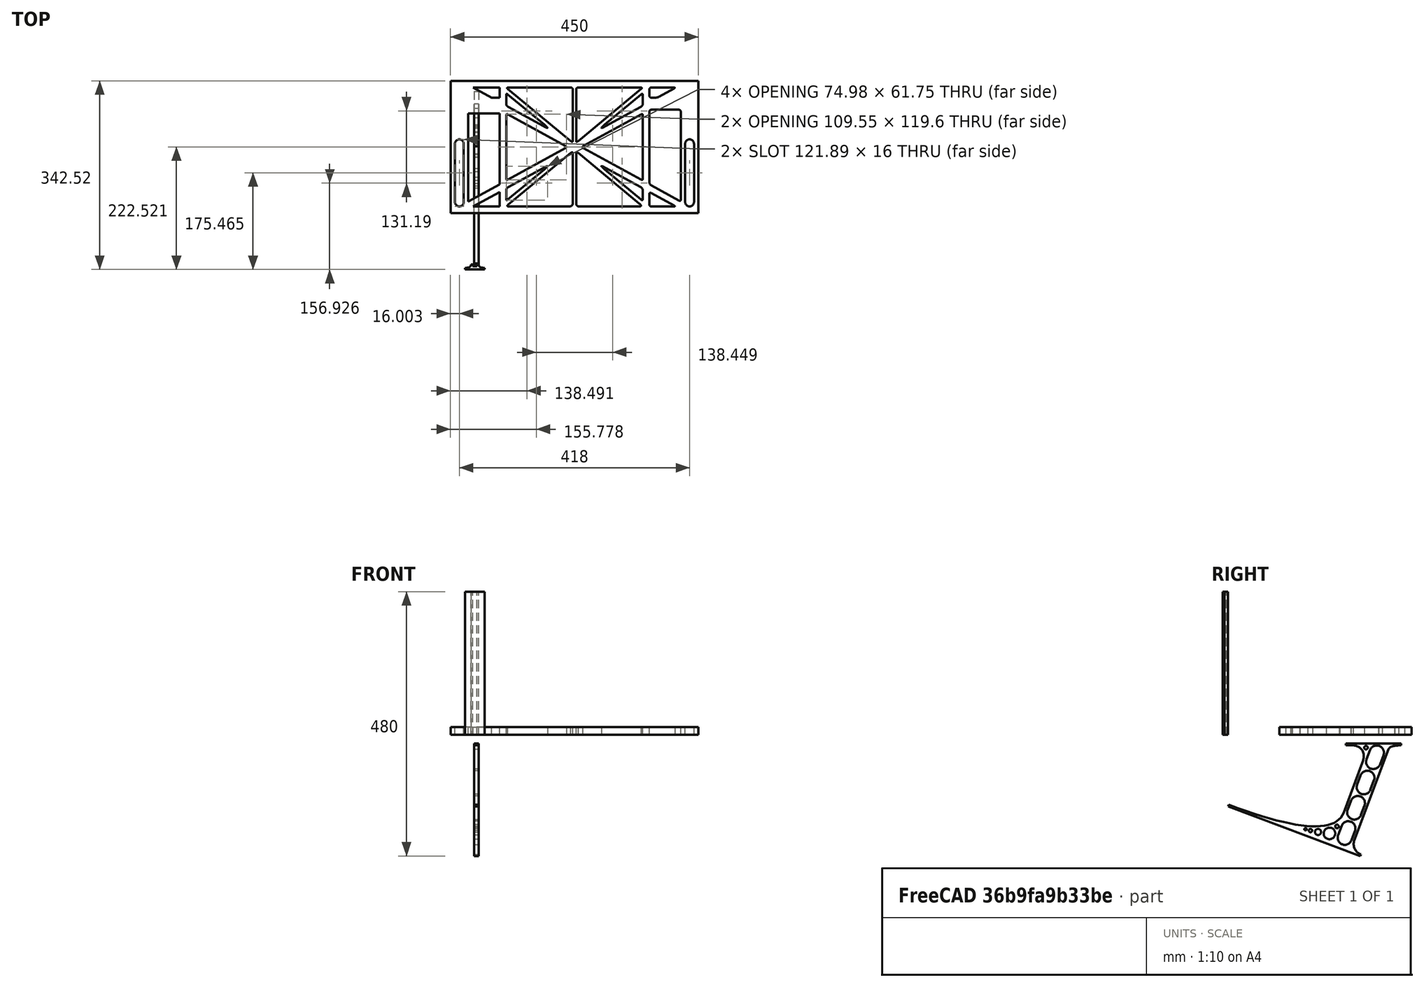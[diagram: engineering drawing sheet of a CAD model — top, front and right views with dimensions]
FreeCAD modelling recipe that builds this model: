
FCSTD DOCUMENT  (FreeCAD 0.19R0.19.2)
Label: laptopStand112
License: All rights reserved
LicenseURL: http://en.wikipedia.org/wiki/All_rights_reserved
objects: Sketcher::SketchObject×3, Part::Extrusion×3
note: 6 computed .brp shape members not serialized (recipe doc carries the construction recipe); baked Part::Feature solids carry a one-line shape summary decoded from their .brp

FEATURE [Sketcher::SketchObject] Sketch
  FullyConstrained = true
  sketch-geometry (310):
    g0: LineSegment StartX=-10.9272 StartY=-82.7794 StartZ=0 EndX=46.0728 EndY=-51.4823 EndZ=0
    g1: LineSegment StartX=-10.9272 StartY=77.3346 StartZ=0 EndX=-10.9272 EndY=-82.7794 EndZ=0
    g2: LineSegment StartX=-1.92719 StartY=-91.7794 StartZ=0 EndX=46.0728 EndY=-91.7794 EndZ=0
    g3: LineSegment StartX=46.0728 StartY=-65.424 StartZ=0 EndX=-1.92719 EndY=-91.7794 EndZ=0
    g4: LineSegment StartX=46.0728 StartY=-65.424 StartZ=0 EndX=46.0728 EndY=-91.7794 EndZ=0
    g5: LineSegment StartX=46.0728 StartY=77.3346 StartZ=0 EndX=46.0728 EndY=-51.4823 EndZ=0
    g6: LineSegment StartX=-42.9272 StartY=136.221 StartZ=0 EndX=-42.9272 EndY=-103.779 EndZ=0
    g7: LineSegment StartX=407.073 StartY=136.221 StartZ=0 EndX=407.073 EndY=-103.779 EndZ=0
    g8: ArcOfCircle CenterX=-26.9272 CenterY=22.1087 CenterZ=0 NormalX=0 NormalY=0 NormalZ=1 AngleXU=0 Radius=8 StartAngle=1e-16 EndAngle=3.14159
    g9: ArcOfCircle CenterX=-26.9272 CenterY=-83.7794 CenterZ=0 NormalX=0 NormalY=0 NormalZ=1 AngleXU=0 Radius=8 StartAngle=3.14159 EndAngle=6.28319
    g10: LineSegment StartX=-34.9272 StartY=22.1087 StartZ=0 EndX=-34.9272 EndY=-83.7794 EndZ=0
    g11: LineSegment StartX=-18.9272 StartY=22.1087 StartZ=0 EndX=-18.9272 EndY=-83.7794 EndZ=0
    g12: ArcOfCircle CenterX=391.073 CenterY=22.1087 CenterZ=0 NormalX=0 NormalY=0 NormalZ=1 AngleXU=0 Radius=8 StartAngle=-4.4e-15 EndAngle=3.14159
    g13: LineSegment StartX=399.073 StartY=22.1087 StartZ=0 EndX=399.073 EndY=-83.7794 EndZ=0
    g14: LineSegment StartX=383.073 StartY=22.1087 StartZ=0 EndX=383.073 EndY=-83.7794 EndZ=0
    g15: ArcOfCircle CenterX=391.073 CenterY=-83.7794 CenterZ=0 NormalX=0 NormalY=0 NormalZ=1 AngleXU=0 Radius=8 StartAngle=3.14159 EndAngle=6.28319
    g16: Circle CenterX=175.022 CenterY=27.0628 CenterZ=0 NormalX=0 NormalY=0 NormalZ=1 AngleXU=0 Radius=1
    g17: Circle CenterX=179.022 CenterY=24.8665 CenterZ=0 NormalX=0 NormalY=0 NormalZ=1 AngleXU=0 Radius=1
    g18: Circle CenterX=179.022 CenterY=27.0628 CenterZ=0 NormalX=0 NormalY=0 NormalZ=1 AngleXU=0 Radius=1
    g19: BSplineCurve PolesCount=3 KnotsCount=2 Degree=2 IsPeriodic=0
    g20: GeomPoint X=175.022 Y=27.0628 Z=0
    g21: GeomPoint X=179.022 Y=27.0628 Z=0
    g22: Circle CenterX=189.124 CenterY=27.0628 CenterZ=0 NormalX=0 NormalY=0 NormalZ=1 AngleXU=0 Radius=1
    g23: Circle CenterX=185.124 CenterY=24.8665 CenterZ=0 NormalX=0 NormalY=0 NormalZ=1 AngleXU=0 Radius=1
    g24: Circle CenterX=185.124 CenterY=27.0628 CenterZ=0 NormalX=0 NormalY=0 NormalZ=1 AngleXU=0 Radius=1
    g25: BSplineCurve PolesCount=3 KnotsCount=2 Degree=2 IsPeriodic=0
    g26: GeomPoint X=189.124 Y=27.0628 Z=0
    g27: GeomPoint X=185.124 Y=27.0628 Z=0
    g28: Circle CenterX=175.022 CenterY=5.37834 CenterZ=0 NormalX=0 NormalY=0 NormalZ=1 AngleXU=0 Radius=1
    g29: Circle CenterX=179.022 CenterY=7.57463 CenterZ=0 NormalX=0 NormalY=0 NormalZ=1 AngleXU=0 Radius=1
    g30: Circle CenterX=179.022 CenterY=5.34704 CenterZ=0 NormalX=0 NormalY=0 NormalZ=1 AngleXU=0 Radius=1
    g31: BSplineCurve PolesCount=3 KnotsCount=2 Degree=2 IsPeriodic=0
    g32: GeomPoint X=175.022 Y=5.37834 Z=0
    g33: GeomPoint X=179.022 Y=5.34704 Z=0
    g34: Circle CenterX=189.124 CenterY=5.37834 CenterZ=0 NormalX=0 NormalY=0 NormalZ=1 AngleXU=0 Radius=1
    g35: Circle CenterX=185.124 CenterY=7.57463 CenterZ=0 NormalX=0 NormalY=0 NormalZ=1 AngleXU=0 Radius=1
    g36: Circle CenterX=185.124 CenterY=5.34704 CenterZ=0 NormalX=0 NormalY=0 NormalZ=1 AngleXU=0 Radius=1
    g37: BSplineCurve PolesCount=3 KnotsCount=2 Degree=2 IsPeriodic=0
    g38: GeomPoint X=189.124 Y=5.37834 Z=0
    g39: GeomPoint X=185.124 Y=5.34704 Z=0
    g40: Circle CenterX=165.871 CenterY=18.1458 CenterZ=0 NormalX=0 NormalY=0 NormalZ=1 AngleXU=0 Radius=1
    g41: Circle CenterX=169.377 CenterY=16.2206 CenterZ=0 NormalX=0 NormalY=0 NormalZ=1 AngleXU=0 Radius=1
    g42: Circle CenterX=165.871 CenterY=14.2954 CenterZ=0 NormalX=0 NormalY=0 NormalZ=1 AngleXU=0 Radius=1
    g43: BSplineCurve PolesCount=3 KnotsCount=2 Degree=2 IsPeriodic=0
    g44: GeomPoint X=165.871 Y=18.1458 Z=0
    g45: GeomPoint X=165.871 Y=14.2954 Z=0
    g46: Circle CenterX=198.275 CenterY=18.1458 CenterZ=0 NormalX=0 NormalY=0 NormalZ=1 AngleXU=0 Radius=1
    g47: Circle CenterX=194.768 CenterY=16.2206 CenterZ=0 NormalX=0 NormalY=0 NormalZ=1 AngleXU=0 Radius=1
    g48: Circle CenterX=198.275 CenterY=14.2954 CenterZ=0 NormalX=0 NormalY=0 NormalZ=1 AngleXU=0 Radius=1
    g49: BSplineCurve PolesCount=3 KnotsCount=2 Degree=2 IsPeriodic=0
    g50: GeomPoint X=198.275 Y=18.1458 Z=0
    g51: GeomPoint X=198.275 Y=14.2954 Z=0
    g52: LineSegment StartX=407.073 StartY=-103.779 StartZ=0 EndX=-42.9272 EndY=-103.779 EndZ=0
    g53: LineSegment StartX=407.073 StartY=136.221 StartZ=0 EndX=-42.9272 EndY=136.221 EndZ=0
    g54: LineSegment StartX=46.0728 StartY=77.3346 StartZ=0 EndX=-10.9272 EndY=77.3346 EndZ=0
    g55: LineSegment StartX=46.0728 StartY=105.865 StartZ=0 EndX=31.5028 EndY=105.865 EndZ=0
    g56: LineSegment StartX=46.0728 StartY=124.221 StartZ=0 EndX=46.0728 EndY=105.865 EndZ=0
    g57: LineSegment StartX=-1.92719 StartY=124.221 StartZ=0 EndX=31.5028 EndY=105.865 EndZ=0
    g58: LineSegment StartX=46.0728 StartY=124.221 StartZ=0 EndX=-1.92719 EndY=124.221 EndZ=0
    g59: Circle CenterX=125.607 CenterY=54.1951 CenterZ=0 NormalX=0 NormalY=0 NormalZ=1 AngleXU=0 Radius=1
    g60: Circle CenterX=139.632 CenterY=46.4944 CenterZ=0 NormalX=0 NormalY=0 NormalZ=1 AngleXU=0 Radius=1
    g61: Circle CenterX=127.326 CenterY=56.7187 CenterZ=0 NormalX=0 NormalY=0 NormalZ=1 AngleXU=0 Radius=1
    g62: BSplineCurve PolesCount=3 KnotsCount=2 Degree=2 IsPeriodic=0
    g63: GeomPoint X=125.607 Y=54.1951 Z=0
    g64: GeomPoint X=127.326 Y=56.7187 Z=0
    g65: Circle CenterX=236.821 CenterY=56.7187 CenterZ=0 NormalX=0 NormalY=0 NormalZ=1 AngleXU=0 Radius=1
    g66: Circle CenterX=224.513 CenterY=46.4944 CenterZ=0 NormalX=0 NormalY=0 NormalZ=1 AngleXU=0 Radius=1
    g67: Circle CenterX=238.538 CenterY=54.1951 CenterZ=0 NormalX=0 NormalY=0 NormalZ=1 AngleXU=0 Radius=1
    g68: BSplineCurve PolesCount=3 KnotsCount=2 Degree=2 IsPeriodic=0
    g69: GeomPoint X=236.821 Y=56.7187 Z=0
    g70: GeomPoint X=238.538 Y=54.1951 Z=0
    g71: Circle CenterX=238.538 CenterY=-21.7539 CenterZ=0 NormalX=0 NormalY=0 NormalZ=1 AngleXU=0 Radius=1
    g72: Circle CenterX=224.513 CenterY=-14.0532 CenterZ=0 NormalX=0 NormalY=0 NormalZ=1 AngleXU=0 Radius=1
    g73: Circle CenterX=236.821 CenterY=-24.2775 CenterZ=0 NormalX=0 NormalY=0 NormalZ=1 AngleXU=0 Radius=1
    g74: BSplineCurve PolesCount=3 KnotsCount=2 Degree=2 IsPeriodic=0
    g75: GeomPoint X=238.538 Y=-21.7539 Z=0
    g76: GeomPoint X=236.821 Y=-24.2775 Z=0
    g77: Circle CenterX=125.607 CenterY=-21.7539 CenterZ=0 NormalX=0 NormalY=0 NormalZ=1 AngleXU=0 Radius=1
    g78: Circle CenterX=139.632 CenterY=-14.0532 CenterZ=0 NormalX=0 NormalY=0 NormalZ=1 AngleXU=0 Radius=1
    g79: Circle CenterX=127.325 CenterY=-24.2775 CenterZ=0 NormalX=0 NormalY=0 NormalZ=1 AngleXU=0 Radius=1
    g80: BSplineCurve PolesCount=3 KnotsCount=2 Degree=2 IsPeriodic=0
    g81: GeomPoint X=125.607 Y=-21.7539 Z=0
    g82: GeomPoint X=127.325 Y=-24.2775 Z=0
    g83: Circle CenterX=302.996 CenterY=111.695 CenterZ=0 NormalX=0 NormalY=0 NormalZ=1 AngleXU=0 Radius=1
    g84: Circle CenterX=306.073 CenterY=114.251 CenterZ=0 NormalX=0 NormalY=0 NormalZ=1 AngleXU=0 Radius=1
    g85: Circle CenterX=306.073 CenterY=110.251 CenterZ=0 NormalX=0 NormalY=0 NormalZ=1 AngleXU=0 Radius=1
    g86: BSplineCurve PolesCount=3 KnotsCount=2 Degree=2 IsPeriodic=0
    g87: GeomPoint X=302.996 Y=111.695 Z=0
    g88: GeomPoint X=306.073 Y=110.251 Z=0
    g89: Circle CenterX=306.073 CenterY=95.2763 CenterZ=0 NormalX=0 NormalY=0 NormalZ=1 AngleXU=0 Radius=1
    g90: Circle CenterX=306.073 CenterY=91.2763 CenterZ=0 NormalX=0 NormalY=0 NormalZ=1 AngleXU=0 Radius=1
    g91: Circle CenterX=302.567 CenterY=89.3511 CenterZ=0 NormalX=0 NormalY=0 NormalZ=1 AngleXU=0 Radius=1
    g92: BSplineCurve PolesCount=3 KnotsCount=2 Degree=2 IsPeriodic=0
    g93: GeomPoint X=306.073 Y=95.2763 Z=0
    g94: GeomPoint X=302.567 Y=89.3511 Z=0
    g95: LineSegment StartX=306.073 StartY=110.251 StartZ=0 EndX=306.073 EndY=95.2763 EndZ=0
    g96: LineSegment StartX=302.996 StartY=111.695 StartZ=0 EndX=236.821 EndY=56.7187 EndZ=0
    g97: LineSegment StartX=238.538 StartY=54.1951 StartZ=0 EndX=302.567 EndY=89.3511 EndZ=0
    g98: Circle CenterX=61.1496 CenterY=111.695 CenterZ=0 NormalX=0 NormalY=0 NormalZ=1 AngleXU=0 Radius=1
    g99: Circle CenterX=58.0728 CenterY=114.251 CenterZ=0 NormalX=0 NormalY=0 NormalZ=1 AngleXU=0 Radius=1
    g100: Circle CenterX=58.0728 CenterY=110.251 CenterZ=0 NormalX=0 NormalY=0 NormalZ=1 AngleXU=0 Radius=1
    g101: BSplineCurve PolesCount=3 KnotsCount=2 Degree=2 IsPeriodic=0
    g102: GeomPoint X=61.1496 Y=111.695 Z=0
    g103: GeomPoint X=58.0728 Y=110.251 Z=0
    g104: Circle CenterX=61.5791 CenterY=89.3511 CenterZ=0 NormalX=0 NormalY=0 NormalZ=1 AngleXU=0 Radius=1
    g105: Circle CenterX=58.0728 CenterY=91.2763 CenterZ=0 NormalX=0 NormalY=0 NormalZ=1 AngleXU=0 Radius=1
    g106: Circle CenterX=58.0728 CenterY=95.2763 CenterZ=0 NormalX=0 NormalY=0 NormalZ=1 AngleXU=0 Radius=1
    g107: BSplineCurve PolesCount=3 KnotsCount=2 Degree=2 IsPeriodic=0
    g108: GeomPoint X=61.5791 Y=89.3511 Z=0
    g109: GeomPoint X=58.0728 Y=95.2763 Z=0
    g110: LineSegment StartX=58.0728 StartY=110.251 StartZ=0 EndX=58.0728 EndY=95.2763 EndZ=0
    g111: LineSegment StartX=61.1496 StartY=111.695 StartZ=0 EndX=127.326 EndY=56.7187 EndZ=0
    g112: LineSegment StartX=125.607 StartY=54.1951 StartZ=0 EndX=61.5791 EndY=89.3511 EndZ=0
    g113: Circle CenterX=61.5791 CenterY=-56.9099 CenterZ=0 NormalX=0 NormalY=0 NormalZ=1 AngleXU=0 Radius=1
    g114: Circle CenterX=58.0728 CenterY=-58.8351 CenterZ=0 NormalX=0 NormalY=0 NormalZ=1 AngleXU=0 Radius=1
    g115: Circle CenterX=58.0728 CenterY=-62.8351 CenterZ=0 NormalX=0 NormalY=0 NormalZ=1 AngleXU=0 Radius=1
    g116: BSplineCurve PolesCount=3 KnotsCount=2 Degree=2 IsPeriodic=0
    g117: GeomPoint X=61.5791 Y=-56.9099 Z=0
    g118: GeomPoint X=58.0728 Y=-62.8351 Z=0
    g119: Circle CenterX=58.0728 CenterY=-77.8102 CenterZ=0 NormalX=0 NormalY=0 NormalZ=1 AngleXU=0 Radius=1
    g120: Circle CenterX=58.0728 CenterY=-81.8102 CenterZ=0 NormalX=0 NormalY=0 NormalZ=1 AngleXU=0 Radius=1
    g121: Circle CenterX=61.1496 CenterY=-79.2541 CenterZ=0 NormalX=0 NormalY=0 NormalZ=1 AngleXU=0 Radius=1
    g122: BSplineCurve PolesCount=3 KnotsCount=2 Degree=2 IsPeriodic=0
    g123: GeomPoint X=58.0728 Y=-77.8102 Z=0
    g124: GeomPoint X=61.1496 Y=-79.2541 Z=0
    g125: LineSegment StartX=58.0728 StartY=-62.8351 StartZ=0 EndX=58.0728 EndY=-77.8102 EndZ=0
    g126: LineSegment StartX=61.1496 StartY=-79.2541 StartZ=0 EndX=127.325 EndY=-24.2775 EndZ=0
    g127: LineSegment StartX=125.607 StartY=-21.7539 StartZ=0 EndX=61.5791 EndY=-56.9099 EndZ=0
    g128: Circle CenterX=302.567 CenterY=-56.9099 CenterZ=0 NormalX=0 NormalY=0 NormalZ=1 AngleXU=0 Radius=1
    g129: Circle CenterX=306.073 CenterY=-58.8351 CenterZ=0 NormalX=0 NormalY=0 NormalZ=1 AngleXU=0 Radius=1
    g130: Circle CenterX=306.073 CenterY=-62.8351 CenterZ=0 NormalX=0 NormalY=0 NormalZ=1 AngleXU=0 Radius=1
    g131: BSplineCurve PolesCount=3 KnotsCount=2 Degree=2 IsPeriodic=0
    g132: GeomPoint X=302.567 Y=-56.9099 Z=0
    g133: GeomPoint X=306.073 Y=-62.8351 Z=0
    g134: Circle CenterX=302.996 CenterY=-79.2541 CenterZ=0 NormalX=0 NormalY=0 NormalZ=1 AngleXU=0 Radius=1
    g135: Circle CenterX=306.073 CenterY=-81.8102 CenterZ=0 NormalX=0 NormalY=0 NormalZ=1 AngleXU=0 Radius=1
    g136: Circle CenterX=306.073 CenterY=-77.8102 CenterZ=0 NormalX=0 NormalY=0 NormalZ=1 AngleXU=0 Radius=1
    g137: BSplineCurve PolesCount=3 KnotsCount=2 Degree=2 IsPeriodic=0
    g138: GeomPoint X=302.996 Y=-79.2541 Z=0
    g139: GeomPoint X=306.073 Y=-77.8102 Z=0
    g140: LineSegment StartX=306.073 StartY=-62.8351 StartZ=0 EndX=306.073 EndY=-77.8102 EndZ=0
    g141: LineSegment StartX=302.996 StartY=-79.2541 StartZ=0 EndX=236.821 EndY=-24.2775 EndZ=0
    g142: LineSegment StartX=238.538 StartY=-21.7539 StartZ=0 EndX=302.567 EndY=-56.9099 EndZ=0
    g143: Circle CenterX=61.6457 CenterY=-88.8112 CenterZ=0 NormalX=0 NormalY=0 NormalZ=1 AngleXU=0 Radius=1
    g144: Circle CenterX=58.0728 CenterY=-91.7794 CenterZ=0 NormalX=0 NormalY=0 NormalZ=1 AngleXU=0 Radius=1
    g145: Circle CenterX=63.9135 CenterY=-91.7794 CenterZ=0 NormalX=0 NormalY=0 NormalZ=1 AngleXU=0 Radius=1
    g146: BSplineCurve PolesCount=3 KnotsCount=2 Degree=2 IsPeriodic=0
    g147: GeomPoint X=61.6457 Y=-88.8112 Z=0
    g148: GeomPoint X=63.9135 Y=-91.7794 Z=0
    g149: Circle CenterX=179.022 CenterY=-85.8163 CenterZ=0 NormalX=0 NormalY=0 NormalZ=1 AngleXU=0 Radius=1
    g150: Circle CenterX=179.022 CenterY=-91.7794 CenterZ=0 NormalX=0 NormalY=0 NormalZ=1 AngleXU=0 Radius=1
    g151: Circle CenterX=171.895 CenterY=-91.7794 CenterZ=0 NormalX=0 NormalY=0 NormalZ=1 AngleXU=0 Radius=1
    g152: BSplineCurve PolesCount=3 KnotsCount=2 Degree=2 IsPeriodic=0
    g153: GeomPoint X=179.022 Y=-85.8163 Z=0
    g154: GeomPoint X=171.895 Y=-91.7794 Z=0
    g155: Circle CenterX=185.124 CenterY=-86.2028 CenterZ=0 NormalX=0 NormalY=0 NormalZ=1 AngleXU=0 Radius=1
    g156: Circle CenterX=185.124 CenterY=-91.7794 CenterZ=0 NormalX=0 NormalY=0 NormalZ=1 AngleXU=0 Radius=1
    g157: Circle CenterX=191.747 CenterY=-91.7794 CenterZ=0 NormalX=0 NormalY=0 NormalZ=1 AngleXU=0 Radius=1
    g158: BSplineCurve PolesCount=3 KnotsCount=2 Degree=2 IsPeriodic=0
    g159: GeomPoint X=185.124 Y=-86.2028 Z=0
    g160: GeomPoint X=191.747 Y=-91.7794 Z=0
    g161: Circle CenterX=299.888 CenterY=-86.6413 CenterZ=0 NormalX=0 NormalY=0 NormalZ=1 AngleXU=0 Radius=1
    g162: Circle CenterX=306.073 CenterY=-91.7794 CenterZ=0 NormalX=0 NormalY=0 NormalZ=1 AngleXU=0 Radius=1
    g163: Circle CenterX=298.776 CenterY=-91.7794 CenterZ=0 NormalX=0 NormalY=0 NormalZ=1 AngleXU=0 Radius=1
    g164: BSplineCurve PolesCount=3 KnotsCount=2 Degree=2 IsPeriodic=0
    g165: GeomPoint X=299.888 Y=-86.6413 Z=0
    g166: GeomPoint X=298.776 Y=-91.7794 Z=0
    g167: LineSegment StartX=189.124 StartY=5.37834 StartZ=0 EndX=299.888 EndY=-86.6413 EndZ=0
    g168: LineSegment StartX=298.776 StartY=-91.7794 StartZ=0 EndX=191.747 EndY=-91.7794 EndZ=0
    g169: LineSegment StartX=185.124 StartY=-86.2028 StartZ=0 EndX=185.124 EndY=5.34704 EndZ=0
    g170: LineSegment StartX=179.022 StartY=5.34704 StartZ=0 EndX=179.022 EndY=-85.8163 EndZ=0
    g171: LineSegment StartX=171.895 StartY=-91.7794 StartZ=0 EndX=63.9135 EndY=-91.7794 EndZ=0
    g172: LineSegment StartX=61.6457 StartY=-88.8112 StartZ=0 EndX=175.022 EndY=5.37834 EndZ=0
    g173: Circle CenterX=302.073 CenterY=124.221 CenterZ=0 NormalX=0 NormalY=0 NormalZ=1 AngleXU=0 Radius=1
    g174: Circle CenterX=306.073 CenterY=124.221 CenterZ=0 NormalX=0 NormalY=0 NormalZ=1 AngleXU=0 Radius=1
    g175: Circle CenterX=302.996 CenterY=121.665 CenterZ=0 NormalX=0 NormalY=0 NormalZ=1 AngleXU=0 Radius=1
    g176: BSplineCurve PolesCount=3 KnotsCount=2 Degree=2 IsPeriodic=0
    g177: GeomPoint X=302.073 Y=124.221 Z=0
    g178: GeomPoint X=302.996 Y=121.665 Z=0
    g179: Circle CenterX=189.124 CenterY=124.221 CenterZ=0 NormalX=0 NormalY=0 NormalZ=1 AngleXU=0 Radius=1
    g180: Circle CenterX=185.124 CenterY=124.221 CenterZ=0 NormalX=0 NormalY=0 NormalZ=1 AngleXU=0 Radius=1
    g181: Circle CenterX=185.124 CenterY=120.221 CenterZ=0 NormalX=0 NormalY=0 NormalZ=1 AngleXU=0 Radius=1
    g182: BSplineCurve PolesCount=3 KnotsCount=2 Degree=2 IsPeriodic=0
    g183: GeomPoint X=189.124 Y=124.221 Z=0
    g184: GeomPoint X=185.124 Y=120.221 Z=0
    g185: Circle CenterX=175.022 CenterY=124.221 CenterZ=0 NormalX=0 NormalY=0 NormalZ=1 AngleXU=0 Radius=1
    g186: Circle CenterX=179.022 CenterY=124.221 CenterZ=0 NormalX=0 NormalY=0 NormalZ=1 AngleXU=0 Radius=1
    g187: Circle CenterX=179.022 CenterY=120.221 CenterZ=0 NormalX=0 NormalY=0 NormalZ=1 AngleXU=0 Radius=1
    g188: BSplineCurve PolesCount=3 KnotsCount=2 Degree=2 IsPeriodic=0
    g189: GeomPoint X=175.022 Y=124.221 Z=0
    g190: GeomPoint X=179.022 Y=120.221 Z=0
    g191: Circle CenterX=62.0728 CenterY=124.221 CenterZ=0 NormalX=0 NormalY=0 NormalZ=1 AngleXU=0 Radius=1
    g192: Circle CenterX=58.0728 CenterY=124.221 CenterZ=0 NormalX=0 NormalY=0 NormalZ=1 AngleXU=0 Radius=1
    g193: Circle CenterX=61.1496 CenterY=121.665 CenterZ=0 NormalX=0 NormalY=0 NormalZ=1 AngleXU=0 Radius=1
    g194: BSplineCurve PolesCount=3 KnotsCount=2 Degree=2 IsPeriodic=0
    g195: GeomPoint X=62.0728 Y=124.221 Z=0
    g196: GeomPoint X=61.1496 Y=121.665 Z=0
    g197: LineSegment StartX=62.0728 StartY=124.221 StartZ=0 EndX=175.022 EndY=124.221 EndZ=0
    g198: LineSegment StartX=179.022 StartY=120.221 StartZ=0 EndX=179.022 EndY=27.0628 EndZ=0
    g199: LineSegment StartX=185.124 StartY=27.0628 StartZ=0 EndX=185.124 EndY=120.221 EndZ=0
    g200: LineSegment StartX=189.124 StartY=124.221 StartZ=0 EndX=302.073 EndY=124.221 EndZ=0
    g201: LineSegment StartX=302.996 StartY=121.665 StartZ=0 EndX=189.124 EndY=27.0628 EndZ=0
    g202: LineSegment StartX=175.022 StartY=27.0628 StartZ=0 EndX=61.1496 EndY=121.665 EndZ=0
    g203: Circle CenterX=61.5791 CenterY=75.4095 CenterZ=0 NormalX=0 NormalY=0 NormalZ=1 AngleXU=0 Radius=1
    g204: Circle CenterX=58.0728 CenterY=77.3346 CenterZ=0 NormalX=0 NormalY=0 NormalZ=1 AngleXU=0 Radius=1
    g205: Circle CenterX=58.0728 CenterY=73.3346 CenterZ=0 NormalX=0 NormalY=0 NormalZ=1 AngleXU=0 Radius=1
    g206: BSplineCurve PolesCount=3 KnotsCount=2 Degree=2 IsPeriodic=0
    g207: GeomPoint X=61.5791 Y=75.4095 Z=0
    g208: GeomPoint X=58.0728 Y=73.3346 Z=0
    g209: Circle CenterX=58.0728 CenterY=-40.8935 CenterZ=0 NormalX=0 NormalY=0 NormalZ=1 AngleXU=0 Radius=1
    g210: Circle CenterX=58.0728 CenterY=-44.8935 CenterZ=0 NormalX=0 NormalY=0 NormalZ=1 AngleXU=0 Radius=1
    g211: Circle CenterX=61.5791 CenterY=-42.9683 CenterZ=0 NormalX=0 NormalY=0 NormalZ=1 AngleXU=0 Radius=1
    g212: BSplineCurve PolesCount=3 KnotsCount=2 Degree=2 IsPeriodic=0
    g213: GeomPoint X=58.0728 Y=-40.8935 Z=0
    g214: GeomPoint X=61.5791 Y=-42.9683 Z=0
    g215: LineSegment StartX=61.5791 StartY=-42.9683 StartZ=0 EndX=165.871 EndY=14.2954 EndZ=0
    g216: LineSegment StartX=165.871 StartY=18.1458 StartZ=0 EndX=61.5791 EndY=75.4095 EndZ=0
    g217: LineSegment StartX=58.0728 StartY=73.3346 StartZ=0 EndX=58.0728 EndY=-40.8935 EndZ=0
    g218: Circle CenterX=302.567 CenterY=-42.9683 CenterZ=0 NormalX=0 NormalY=0 NormalZ=1 AngleXU=0 Radius=1
    g219: Circle CenterX=306.073 CenterY=-44.8935 CenterZ=0 NormalX=0 NormalY=0 NormalZ=1 AngleXU=0 Radius=1
    g220: Circle CenterX=306.073 CenterY=-40.8935 CenterZ=0 NormalX=0 NormalY=0 NormalZ=1 AngleXU=0 Radius=1
    g221: BSplineCurve PolesCount=3 KnotsCount=2 Degree=2 IsPeriodic=0
    g222: GeomPoint X=302.567 Y=-42.9683 Z=0
    g223: GeomPoint X=306.073 Y=-40.8935 Z=0
    g224: Circle CenterX=306.073 CenterY=73.3346 CenterZ=0 NormalX=0 NormalY=0 NormalZ=1 AngleXU=0 Radius=1
    g225: Circle CenterX=306.073 CenterY=77.3346 CenterZ=0 NormalX=0 NormalY=0 NormalZ=1 AngleXU=0 Radius=1
    g226: Circle CenterX=302.567 CenterY=75.4095 CenterZ=0 NormalX=0 NormalY=0 NormalZ=1 AngleXU=0 Radius=1
    g227: BSplineCurve PolesCount=3 KnotsCount=2 Degree=2 IsPeriodic=0
    g228: GeomPoint X=306.073 Y=73.3346 Z=0
    g229: GeomPoint X=302.567 Y=75.4095 Z=0
    g230: LineSegment StartX=302.567 StartY=-42.9683 StartZ=0 EndX=198.275 EndY=14.2954 EndZ=0
    g231: LineSegment StartX=198.275 StartY=18.1458 StartZ=0 EndX=302.567 EndY=75.4095 EndZ=0
    g232: LineSegment StartX=306.073 StartY=73.3346 StartZ=0 EndX=306.073 EndY=-40.8935 EndZ=0
    g233: LineSegment StartX=322.073 StartY=105.865 StartZ=0 EndX=328.643 EndY=105.865 EndZ=0
    g234: LineSegment StartX=318.073 StartY=120.221 StartZ=0 EndX=318.073 EndY=109.865 EndZ=0
    g235: LineSegment StartX=336.157 StartY=107.779 StartZ=0 EndX=362.567 EndY=122.294 EndZ=0
    g236: Circle CenterX=362.073 CenterY=124.221 CenterZ=0 NormalX=0 NormalY=0 NormalZ=1 AngleXU=0 Radius=1
    g237: Circle CenterX=366.073 CenterY=124.221 CenterZ=0 NormalX=0 NormalY=0 NormalZ=1 AngleXU=0 Radius=1
    g238: Circle CenterX=362.567 CenterY=122.294 CenterZ=0 NormalX=0 NormalY=0 NormalZ=1 AngleXU=0 Radius=1
    g239: BSplineCurve PolesCount=3 KnotsCount=2 Degree=2 IsPeriodic=0
    g240: GeomPoint X=362.073 Y=124.221 Z=0
    g241: GeomPoint X=362.567 Y=122.294 Z=0
    g242: Circle CenterX=322.073 CenterY=124.221 CenterZ=0 NormalX=0 NormalY=0 NormalZ=1 AngleXU=0 Radius=1
    g243: Circle CenterX=318.073 CenterY=124.221 CenterZ=0 NormalX=0 NormalY=0 NormalZ=1 AngleXU=0 Radius=1
    g244: Circle CenterX=318.073 CenterY=120.221 CenterZ=0 NormalX=0 NormalY=0 NormalZ=1 AngleXU=0 Radius=1
    g245: BSplineCurve PolesCount=3 KnotsCount=2 Degree=2 IsPeriodic=0
    g246: GeomPoint X=322.073 Y=124.221 Z=0
    g247: GeomPoint X=318.073 Y=120.221 Z=0
    g248: Circle CenterX=322.073 CenterY=105.865 CenterZ=0 NormalX=0 NormalY=0 NormalZ=1 AngleXU=0 Radius=1
    g249: Circle CenterX=318.073 CenterY=105.865 CenterZ=0 NormalX=0 NormalY=0 NormalZ=1 AngleXU=0 Radius=1
    g250: Circle CenterX=318.073 CenterY=109.865 CenterZ=0 NormalX=0 NormalY=0 NormalZ=1 AngleXU=0 Radius=1
    g251: BSplineCurve PolesCount=3 KnotsCount=2 Degree=2 IsPeriodic=0
    g252: GeomPoint X=322.073 Y=105.865 Z=0
    g253: GeomPoint X=318.073 Y=109.865 Z=0
    g254: Circle CenterX=336.157 CenterY=107.779 CenterZ=0 NormalX=0 NormalY=0 NormalZ=1 AngleXU=0 Radius=1
    g255: Circle CenterX=332.651 CenterY=105.853 CenterZ=0 NormalX=0 NormalY=0 NormalZ=1 AngleXU=0 Radius=1
    g256: Circle CenterX=328.643 CenterY=105.865 CenterZ=0 NormalX=0 NormalY=0 NormalZ=1 AngleXU=0 Radius=1
    g257: BSplineCurve PolesCount=3 KnotsCount=2 Degree=2 IsPeriodic=0
    g258: GeomPoint X=336.157 Y=107.779 Z=0
    g259: GeomPoint X=328.643 Y=105.865 Z=0
    g260: LineSegment StartX=322.073 StartY=124.221 StartZ=0 EndX=362.073 EndY=124.221 EndZ=0
    g261: Circle CenterX=371.567 CenterY=-80.8644 CenterZ=0 NormalX=0 NormalY=0 NormalZ=1 AngleXU=0 Radius=1
    g262: Circle CenterX=375.073 CenterY=-82.7896 CenterZ=0 NormalX=0 NormalY=0 NormalZ=1 AngleXU=0 Radius=1
    g263: Circle CenterX=375.073 CenterY=-78.7896 CenterZ=0 NormalX=0 NormalY=0 NormalZ=1 AngleXU=0 Radius=1
    g264: BSplineCurve PolesCount=3 KnotsCount=2 Degree=2 IsPeriodic=0
    g265: GeomPoint X=371.567 Y=-80.8644 Z=0
    g266: GeomPoint X=375.073 Y=-78.7896 Z=0
    g267: Circle CenterX=321.579 CenterY=-53.4075 CenterZ=0 NormalX=0 NormalY=0 NormalZ=1 AngleXU=0 Radius=1
    g268: Circle CenterX=318.073 CenterY=-51.4823 CenterZ=0 NormalX=0 NormalY=0 NormalZ=1 AngleXU=0 Radius=1
    g269: Circle CenterX=318.073 CenterY=-47.4823 CenterZ=0 NormalX=0 NormalY=0 NormalZ=1 AngleXU=0 Radius=1
    g270: BSplineCurve PolesCount=3 KnotsCount=2 Degree=2 IsPeriodic=0
    g271: GeomPoint X=321.579 Y=-53.4075 Z=0
    g272: GeomPoint X=318.073 Y=-47.4823 Z=0
    g273: Circle CenterX=318.073 CenterY=79.9235 CenterZ=0 NormalX=0 NormalY=0 NormalZ=1 AngleXU=0 Radius=1
    g274: Circle CenterX=318.073 CenterY=83.9235 CenterZ=0 NormalX=0 NormalY=0 NormalZ=1 AngleXU=0 Radius=1
    g275: Circle CenterX=322.073 CenterY=83.9235 CenterZ=0 NormalX=0 NormalY=0 NormalZ=1 AngleXU=0 Radius=1
    g276: BSplineCurve PolesCount=3 KnotsCount=2 Degree=2 IsPeriodic=0
    g277: GeomPoint X=318.073 Y=79.9235 Z=0
    g278: GeomPoint X=322.073 Y=83.9235 Z=0
    g279: Circle CenterX=375.073 CenterY=79.9235 CenterZ=0 NormalX=0 NormalY=0 NormalZ=1 AngleXU=0 Radius=1
    g280: Circle CenterX=375.073 CenterY=83.9235 CenterZ=0 NormalX=0 NormalY=0 NormalZ=1 AngleXU=0 Radius=1
    g281: Circle CenterX=371.073 CenterY=83.9235 CenterZ=0 NormalX=0 NormalY=0 NormalZ=1 AngleXU=0 Radius=1
    g282: BSplineCurve PolesCount=3 KnotsCount=2 Degree=2 IsPeriodic=0
    g283: GeomPoint X=375.073 Y=79.9235 Z=0
    g284: GeomPoint X=371.073 Y=83.9235 Z=0
    g285: LineSegment StartX=322.073 StartY=83.9235 StartZ=0 EndX=371.073 EndY=83.9235 EndZ=0
    g286: LineSegment StartX=375.073 StartY=79.9235 StartZ=0 EndX=375.073 EndY=-78.7896 EndZ=0
    g287: LineSegment StartX=371.567 StartY=-80.8644 StartZ=0 EndX=321.579 EndY=-53.4075 EndZ=0
    g288: LineSegment StartX=318.073 StartY=-47.4823 StartZ=0 EndX=318.073 EndY=79.9235 EndZ=0
    g289: Circle CenterX=321.579 CenterY=-67.3492 CenterZ=0 NormalX=0 NormalY=0 NormalZ=1 AngleXU=0 Radius=1
    g290: Circle CenterX=318.073 CenterY=-65.424 CenterZ=0 NormalX=0 NormalY=0 NormalZ=1 AngleXU=0 Radius=1
    g291: Circle CenterX=318.073 CenterY=-69.424 CenterZ=0 NormalX=0 NormalY=0 NormalZ=1 AngleXU=0 Radius=1
    g292: BSplineCurve PolesCount=3 KnotsCount=2 Degree=2 IsPeriodic=0
    g293: GeomPoint X=321.579 Y=-67.3492 Z=0
    g294: GeomPoint X=318.073 Y=-69.424 Z=0
    g295: Circle CenterX=362.567 CenterY=-89.8542 CenterZ=0 NormalX=0 NormalY=0 NormalZ=1 AngleXU=0 Radius=1
    g296: Circle CenterX=366.073 CenterY=-91.7794 CenterZ=0 NormalX=0 NormalY=0 NormalZ=1 AngleXU=0 Radius=1
    g297: Circle CenterX=362.073 CenterY=-91.7794 CenterZ=0 NormalX=0 NormalY=0 NormalZ=1 AngleXU=0 Radius=1
    g298: BSplineCurve PolesCount=3 KnotsCount=2 Degree=2 IsPeriodic=0
    g299: GeomPoint X=362.567 Y=-89.8542 Z=0
    g300: GeomPoint X=362.073 Y=-91.7794 Z=0
    g301: Circle CenterX=322.073 CenterY=-91.7794 CenterZ=0 NormalX=0 NormalY=0 NormalZ=1 AngleXU=0 Radius=1
    g302: Circle CenterX=318.073 CenterY=-91.7794 CenterZ=0 NormalX=0 NormalY=0 NormalZ=1 AngleXU=0 Radius=1
    g303: Circle CenterX=318.073 CenterY=-87.7794 CenterZ=0 NormalX=0 NormalY=0 NormalZ=1 AngleXU=0 Radius=1
    g304: BSplineCurve PolesCount=3 KnotsCount=2 Degree=2 IsPeriodic=0
    g305: GeomPoint X=322.073 Y=-91.7794 Z=0
    g306: GeomPoint X=318.073 Y=-87.7794 Z=0
    g307: LineSegment StartX=362.567 StartY=-89.8542 StartZ=0 EndX=321.579 EndY=-67.3492 EndZ=0
    g308: LineSegment StartX=318.073 StartY=-69.424 StartZ=0 EndX=318.073 EndY=-87.7794 EndZ=0
    g309: LineSegment StartX=322.073 StartY=-91.7794 StartZ=0 EndX=362.073 EndY=-91.7794 EndZ=0
  constraints (519):
    c: Horizontal(g2)
    c: Coincident(g4,g3)
    c: Coincident(g0,g5)
    c: Block(g4)
    c: Block(g3)
    c: Block(g0)
    c: Block(g1)
    c: Block(g2)
    c: Vertical(g6)
    c: Vertical(g7)
    c: Block(g7)
    c: Block(g6)
    c: Tangent(g8,g11) = 1.5708
    c: Tangent(g8,g10) = -1.5708
    c: Tangent(g10,g9) = -1.5708
    c: Tangent(g11,g9) = 1.5708
    c: Vertical(g10)
    c: Equal(g8,g9)
    c: Block(g11)
    c: Block(g10)
    c: Tangent(g12,g13) = 1.5708
    c: Tangent(g13,g15) = 1.5708
    c: Equal(g12,g15)
    c: Coincident(g14,g12)
    c: Coincident(g14,g15)
    c: Block(g13)
    c: Block(g14)
    c: Weight(g16) = 1
    c: Equal(g16,g17)
    c: Equal(g16,g18)
    c: InternalAlignment(g16,g19)
    c: InternalAlignment(g17,g19)
    c: InternalAlignment(g18,g19)
    c: InternalAlignment(g20,g19)
    c: InternalAlignment(g21,g19)
    c: Weight(g22) = 1
    c: Equal(g22,g23)
    c: Equal(g22,g24)
    c: InternalAlignment(g22,g25)
    c: InternalAlignment(g23,g25)
    c: InternalAlignment(g24,g25)
    c: InternalAlignment(g26,g25)
    c: InternalAlignment(g27,g25)
    c: Block(g25)
    c: Block(g19)
    c: Weight(g28) = 1
    c: Equal(g28,g29)
    c: Equal(g28,g30)
    c: InternalAlignment(g28,g31)
    c: InternalAlignment(g29,g31)
    c: InternalAlignment(g30,g31)
    c: InternalAlignment(g32,g31)
    c: InternalAlignment(g33,g31)
    c: Weight(g34) = 1
    c: Equal(g34,g35)
    c: Equal(g34,g36)
    c: InternalAlignment(g34,g37)
    c: InternalAlignment(g35,g37)
    c: InternalAlignment(g36,g37)
    c: InternalAlignment(g38,g37)
    c: InternalAlignment(g39,g37)
    c: Block(g37)
    c: Block(g31)
    c: Weight(g40) = 1
    c: Equal(g40,g41)
    c: Equal(g40,g42)
    c: InternalAlignment(g40,g43)
    c: InternalAlignment(g41,g43)
    c: InternalAlignment(g42,g43)
    c: InternalAlignment(g44,g43)
    c: InternalAlignment(g45,g43)
    c: Weight(g46) = 1
    c: Equal(g46,g47)
    c: Equal(g46,g48)
    c: InternalAlignment(g46,g49)
    c: InternalAlignment(g47,g49)
    c: InternalAlignment(g48,g49)
    c: InternalAlignment(g50,g49)
    c: InternalAlignment(g51,g49)
    c: Block(g43)
    c: Block(g49)
    c: Coincident(g52,g7)
    c: Coincident(g52,g6)
    c: Horizontal(g52)
    c: Distance(g52) = 450
    c: Coincident(g53,g7)
    c: Coincident(g53,g6)
    c: Horizontal(g53)
    c: Horizontal(g54)
    c: Coincident(g5,g54)
    c: Horizontal(g55)
    c: Vertical(g56)
    c: Block(g56)
    c: Block(g55)
    c: Block(g54)
    c: Distance(g56) = 18.3554
    c: Coincident(g58,g56)
    c: Coincident(g58,g57)
    c: Horizontal(g58)
    c: Block(g58)
    c: Block(g57)
    c: Coincident(g55,g57)
    c: Coincident(g1,g54)
    c: Weight(g59) = 1
    c: Equal(g59,g60)
    c: Equal(g59,g61)
    c: InternalAlignment(g59,g62)
    c: InternalAlignment(g60,g62)
    c: InternalAlignment(g61,g62)
    c: InternalAlignment(g63,g62)
    c: InternalAlignment(g64,g62)
    c: Block(g62)
    c: Weight(g65) = 1
    c: Equal(g65,g66)
    c: Equal(g65,g67)
    c: InternalAlignment(g65,g68)
    c: InternalAlignment(g66,g68)
    c: InternalAlignment(g67,g68)
    c: InternalAlignment(g69,g68)
    c: InternalAlignment(g70,g68)
    c: Block(g68)
    c: Weight(g71) = 1
    c: Equal(g71,g72)
    c: Equal(g71,g73)
    c: InternalAlignment(g71,g74)
    c: InternalAlignment(g72,g74)
    c: InternalAlignment(g73,g74)
    c: InternalAlignment(g75,g74)
    c: InternalAlignment(g76,g74)
    c: Block(g74)
    c: Weight(g77) = 1
    c: Equal(g77,g78)
    c: Equal(g77,g79)
    c: InternalAlignment(g77,g80)
    c: InternalAlignment(g78,g80)
    c: InternalAlignment(g79,g80)
    c: InternalAlignment(g81,g80)
    c: InternalAlignment(g82,g80)
    c: Block(g80)
    c: Weight(g83) = 1
    c: Equal(g83,g84)
    c: Equal(g83,g85)
    c: InternalAlignment(g83,g86)
    c: InternalAlignment(g84,g86)
    c: InternalAlignment(g85,g86)
    c: InternalAlignment(g87,g86)
    c: InternalAlignment(g88,g86)
    c: Weight(g89) = 1
    c: Equal(g89,g90)
    c: Equal(g89,g91)
    c: InternalAlignment(g89,g92)
    c: InternalAlignment(g90,g92)
    c: InternalAlignment(g91,g92)
    c: InternalAlignment(g93,g92)
    c: InternalAlignment(g94,g92)
    c: Block(g86)
    c: Block(g92)
    c: Coincident(g95,g86)
    c: Coincident(g95,g92)
    c: Vertical(g95)
    c: Coincident(g96,g86)
    c: Coincident(g96,g68)
    c: Coincident(g97,g68)
    c: Coincident(g97,g92)
    c: Weight(g98) = 1
    c: Equal(g98,g99)
    c: Equal(g98,g100)
    c: InternalAlignment(g98,g101)
    c: InternalAlignment(g99,g101)
    c: InternalAlignment(g100,g101)
    c: InternalAlignment(g102,g101)
    c: InternalAlignment(g103,g101)
    c: Weight(g104) = 1
    c: Equal(g104,g105)
    c: Equal(g104,g106)
    c: InternalAlignment(g104,g107)
    c: InternalAlignment(g105,g107)
    c: InternalAlignment(g106,g107)
    c: InternalAlignment(g108,g107)
    c: InternalAlignment(g109,g107)
    c: Block(g101)
    c: Block(g107)
    c: Coincident(g110,g101)
    c: Coincident(g110,g107)
    c: Vertical(g110)
    c: Coincident(g111,g101)
    c: Coincident(g111,g62)
    c: Coincident(g112,g62)
    c: Coincident(g112,g107)
    c: Weight(g113) = 1
    c: Equal(g113,g114)
    c: Equal(g113,g115)
    c: InternalAlignment(g113,g116)
    c: InternalAlignment(g114,g116)
    c: InternalAlignment(g115,g116)
    c: InternalAlignment(g117,g116)
    c: InternalAlignment(g118,g116)
    c: Weight(g119) = 1
    c: Equal(g119,g120)
    c: Equal(g119,g121)
    c: InternalAlignment(g119,g122)
    c: InternalAlignment(g120,g122)
    c: InternalAlignment(g121,g122)
    c: InternalAlignment(g123,g122)
    c: InternalAlignment(g124,g122)
    c: Block(g116)
    c: Block(g122)
    c: Coincident(g125,g116)
    c: Coincident(g125,g122)
    c: Vertical(g125)
    c: Coincident(g126,g122)
    c: Coincident(g126,g80)
    c: Coincident(g127,g80)
    c: Coincident(g127,g116)
    c: Weight(g128) = 1
    c: Equal(g128,g129)
    c: Equal(g128,g130)
    c: InternalAlignment(g128,g131)
    c: InternalAlignment(g129,g131)
    c: InternalAlignment(g130,g131)
    c: InternalAlignment(g132,g131)
    c: InternalAlignment(g133,g131)
    c: Weight(g134) = 1
    c: Equal(g134,g135)
    c: Equal(g134,g136)
    c: InternalAlignment(g134,g137)
    c: InternalAlignment(g135,g137)
    c: InternalAlignment(g136,g137)
    c: InternalAlignment(g138,g137)
    c: InternalAlignment(g139,g137)
    c: Block(g131)
    c: Block(g137)
    c: Coincident(g140,g131)
    c: Coincident(g140,g137)
    c: Vertical(g140)
    c: Coincident(g141,g137)
    c: Coincident(g141,g74)
    c: Coincident(g142,g74)
    c: Coincident(g142,g131)
    c: Weight(g143) = 1
    c: Equal(g143,g144)
    c: Equal(g143,g145)
    c: InternalAlignment(g143,g146)
    c: InternalAlignment(g144,g146)
    c: InternalAlignment(g145,g146)
    c: InternalAlignment(g147,g146)
    c: InternalAlignment(g148,g146)
    c: Weight(g149) = 1
    c: Equal(g149,g150)
    c: Equal(g149,g151)
    c: InternalAlignment(g149,g152)
    c: InternalAlignment(g150,g152)
    c: InternalAlignment(g151,g152)
    c: InternalAlignment(g153,g152)
    c: InternalAlignment(g154,g152)
    c: Weight(g155) = 1
    c: Equal(g155,g156)
    c: Equal(g155,g157)
    c: InternalAlignment(g155,g158)
    c: InternalAlignment(g156,g158)
    c: InternalAlignment(g157,g158)
    c: InternalAlignment(g159,g158)
    c: InternalAlignment(g160,g158)
    c: Weight(g161) = 1
    c: Equal(g161,g162)
    c: Equal(g161,g163)
    c: InternalAlignment(g161,g164)
    c: InternalAlignment(g162,g164)
    c: InternalAlignment(g163,g164)
    c: InternalAlignment(g165,g164)
    c: InternalAlignment(g166,g164)
    c: Block(g164)
    c: Block(g158)
    c: Block(g152)
    c: Block(g146)
    c: Coincident(g167,g37)
    c: Coincident(g167,g164)
    c: Coincident(g168,g164)
    c: Coincident(g168,g158)
    c: Horizontal(g168)
    c: Coincident(g169,g158)
    c: Coincident(g169,g37)
    c: Vertical(g169)
    c: Coincident(g170,g31)
    c: Coincident(g170,g152)
    c: Vertical(g170)
    c: Coincident(g171,g152)
    c: Coincident(g171,g146)
    c: Horizontal(g171)
    c: Coincident(g172,g146)
    c: Coincident(g172,g31)
    c: Weight(g173) = 1
    c: Equal(g173,g174)
    c: Equal(g173,g175)
    c: InternalAlignment(g173,g176)
    c: InternalAlignment(g174,g176)
    c: InternalAlignment(g175,g176)
    c: InternalAlignment(g177,g176)
    c: InternalAlignment(g178,g176)
    c: Weight(g179) = 1
    c: Equal(g179,g180)
    c: Equal(g179,g181)
    c: InternalAlignment(g179,g182)
    c: InternalAlignment(g180,g182)
    c: InternalAlignment(g181,g182)
    c: InternalAlignment(g183,g182)
    c: InternalAlignment(g184,g182)
    c: Weight(g185) = 1
    c: Equal(g185,g186)
    c: Equal(g185,g187)
    c: InternalAlignment(g185,g188)
    c: InternalAlignment(g186,g188)
    c: InternalAlignment(g187,g188)
    c: InternalAlignment(g189,g188)
    c: InternalAlignment(g190,g188)
    c: Weight(g191) = 1
    c: Equal(g191,g192)
    c: Equal(g191,g193)
    c: InternalAlignment(g191,g194)
    c: InternalAlignment(g192,g194)
    c: InternalAlignment(g193,g194)
    c: InternalAlignment(g195,g194)
    c: InternalAlignment(g196,g194)
    c: Block(g194)
    c: Block(g188)
    c: Block(g182)
    c: Block(g176)
    c: Coincident(g197,g194)
    c: Coincident(g197,g188)
    c: Horizontal(g197)
    c: Coincident(g198,g188)
    c: Coincident(g198,g19)
    c: Vertical(g198)
    c: Coincident(g199,g25)
    c: Coincident(g199,g182)
    c: Vertical(g199)
    c: Coincident(g200,g182)
    c: Coincident(g200,g176)
    c: Horizontal(g200)
    c: Coincident(g201,g176)
    c: Coincident(g201,g25)
    c: Coincident(g202,g19)
    c: Weight(g203) = 1
    c: Equal(g203,g204)
    c: Equal(g203,g205)
    c: InternalAlignment(g203,g206)
    c: InternalAlignment(g204,g206)
    c: InternalAlignment(g205,g206)
    c: InternalAlignment(g207,g206)
    c: InternalAlignment(g208,g206)
    c: Weight(g209) = 1
    c: Equal(g209,g210)
    c: Equal(g209,g211)
    c: InternalAlignment(g209,g212)
    c: InternalAlignment(g210,g212)
    c: InternalAlignment(g211,g212)
    c: InternalAlignment(g213,g212)
    c: InternalAlignment(g214,g212)
    c: Block(g212)
    c: Block(g206)
    c: Coincident(g215,g212)
    c: Coincident(g215,g43)
    c: Coincident(g216,g43)
    c: Coincident(g216,g206)
    c: Coincident(g217,g206)
    c: Coincident(g217,g212)
    c: Vertical(g217)
    c: Weight(g218) = 1
    c: Equal(g218,g219)
    c: Equal(g218,g220)
    c: InternalAlignment(g218,g221)
    c: InternalAlignment(g219,g221)
    c: InternalAlignment(g220,g221)
    c: InternalAlignment(g222,g221)
    c: InternalAlignment(g223,g221)
    c: Weight(g224) = 1
    c: Equal(g224,g225)
    c: Equal(g224,g226)
    c: InternalAlignment(g224,g227)
    c: InternalAlignment(g225,g227)
    c: InternalAlignment(g226,g227)
    c: InternalAlignment(g228,g227)
    c: InternalAlignment(g229,g227)
    c: Block(g227)
    c: Block(g221)
    c: Coincident(g230,g221)
    c: Coincident(g230,g49)
    c: Coincident(g231,g49)
    c: Coincident(g231,g227)
    c: Coincident(g232,g227)
    c: Coincident(g232,g221)
    c: Vertical(g232)
    c: Horizontal(g233)
    c: Block(g233)
    c: Vertical(g234)
    c: Block(g234)
    c: Block(g235)
    c: Weight(g236) = 1
    c: Equal(g236,g237)
    c: Equal(g236,g238)
    c: InternalAlignment(g236,g239)
    c: InternalAlignment(g237,g239)
    c: InternalAlignment(g238,g239)
    c: InternalAlignment(g240,g239)
    c: InternalAlignment(g241,g239)
    c: Weight(g242) = 1
    c: Equal(g242,g243)
    c: Equal(g242,g244)
    c: InternalAlignment(g242,g245)
    c: InternalAlignment(g243,g245)
    c: InternalAlignment(g244,g245)
    c: InternalAlignment(g246,g245)
    c: InternalAlignment(g247,g245)
    c: Weight(g248) = 1
    c: Equal(g248,g249)
    c: Equal(g248,g250)
    c: InternalAlignment(g248,g251)
    c: InternalAlignment(g249,g251)
    c: InternalAlignment(g250,g251)
    c: InternalAlignment(g252,g251)
    c: InternalAlignment(g253,g251)
    c: Weight(g254) = 1
    c: Equal(g254,g255)
    c: Equal(g254,g256)
    c: InternalAlignment(g254,g257)
    c: InternalAlignment(g255,g257)
    c: InternalAlignment(g256,g257)
    c: InternalAlignment(g258,g257)
    c: InternalAlignment(g259,g257)
    c: Block(g239)
    c: Block(g245)
    c: Block(g251)
    c: Block(g257)
    c: Coincident(g260,g245)
    c: Coincident(g260,g239)
    c: Horizontal(g260)
    c: Block(g202)
    c: Weight(g261) = 1
    c: Equal(g261,g262)
    c: Equal(g261,g263)
    c: InternalAlignment(g261,g264)
    c: InternalAlignment(g262,g264)
    c: InternalAlignment(g263,g264)
    c: InternalAlignment(g265,g264)
    c: InternalAlignment(g266,g264)
    c: Weight(g267) = 1
    c: Equal(g267,g268)
    c: Equal(g267,g269)
    c: InternalAlignment(g267,g270)
    c: InternalAlignment(g268,g270)
    c: InternalAlignment(g269,g270)
    c: InternalAlignment(g271,g270)
    c: InternalAlignment(g272,g270)
    c: Weight(g273) = 1
    c: Equal(g273,g274)
    c: Equal(g273,g275)
    c: InternalAlignment(g273,g276)
    c: InternalAlignment(g274,g276)
    c: InternalAlignment(g275,g276)
    c: InternalAlignment(g277,g276)
    c: InternalAlignment(g278,g276)
    c: Weight(g279) = 1
    c: Equal(g279,g280)
    c: Equal(g279,g281)
    c: InternalAlignment(g279,g282)
    c: InternalAlignment(g280,g282)
    c: InternalAlignment(g281,g282)
    c: InternalAlignment(g283,g282)
    c: InternalAlignment(g284,g282)
    c: Block(g264)
    c: Block(g270)
    c: Block(g276)
    c: Block(g282)
    c: Coincident(g285,g276)
    c: Coincident(g285,g282)
    c: Horizontal(g285)
    c: Coincident(g286,g282)
    c: Coincident(g286,g264)
    c: Vertical(g286)
    c: Coincident(g287,g264)
    c: Coincident(g287,g270)
    c: Coincident(g288,g270)
    c: Coincident(g288,g276)
    c: Vertical(g288)
    c: Weight(g289) = 1
    c: Equal(g289,g290)
    c: Equal(g289,g291)
    c: InternalAlignment(g289,g292)
    c: InternalAlignment(g290,g292)
    c: InternalAlignment(g291,g292)
    c: InternalAlignment(g293,g292)
    c: InternalAlignment(g294,g292)
    c: Weight(g295) = 1
    c: Equal(g295,g296)
    c: Equal(g295,g297)
    c: InternalAlignment(g295,g298)
    c: InternalAlignment(g296,g298)
    c: InternalAlignment(g297,g298)
    c: InternalAlignment(g299,g298)
    c: InternalAlignment(g300,g298)
    c: Weight(g301) = 1
    c: Equal(g301,g302)
    c: Equal(g301,g303)
    c: InternalAlignment(g301,g304)
    c: InternalAlignment(g302,g304)
    c: InternalAlignment(g303,g304)
    c: InternalAlignment(g305,g304)
    c: InternalAlignment(g306,g304)
    c: Block(g304)
    c: Block(g298)
    c: Block(g292)
    c: Coincident(g307,g298)
    c: Coincident(g307,g292)
    c: Coincident(g308,g292)
    c: Coincident(g308,g304)
    c: Vertical(g308)
    c: Coincident(g309,g304)
    c: Coincident(g309,g298)
    c: Horizontal(g309)
FEATURE [Sketcher::SketchObject] Sketch001
  FullyConstrained = true
  MapMode = 4
  Placement = pos=(0,0,0) rot=(0.57735,0.57735,0.57735;2.0944rad)
  Support = -> [Sketch]
  sketch-geometry (46):
    g0: BSplineCurve PolesCount=3 KnotsCount=2 Degree=2 IsPeriodic=0
    g1: ArcOfCircle CenterX=73.1223 CenterY=-32.291 CenterZ=0 NormalX=0 NormalY=0 NormalZ=1 AngleXU=0 Radius=13 StartAngle=5.92268 EndAngle=9.06428
    g2: ArcOfCircle CenterX=66.7816 CenterY=-49.1439 CenterZ=0 NormalX=0 NormalY=0 NormalZ=1 AngleXU=0 Radius=13 StartAngle=2.78068 EndAngle=5.92131
    g3: ArcOfCircle CenterX=55.9263 CenterY=-78.1807 CenterZ=0 NormalX=0 NormalY=0 NormalZ=1 AngleXU=0 Radius=13 StartAngle=5.92268 EndAngle=9.06428
    g4: ArcOfCircle CenterX=49.5884 CenterY=-95.0342 CenterZ=0 NormalX=0 NormalY=0 NormalZ=1 AngleXU=0 Radius=13 StartAngle=2.78068 EndAngle=5.92131
    g5: ArcOfCircle CenterX=38.7206 CenterY=-124.067 CenterZ=0 NormalX=0 NormalY=0 NormalZ=1 AngleXU=0 Radius=13 StartAngle=5.92268 EndAngle=9.06428
    g6: ArcOfCircle CenterX=32.3875 CenterY=-140.92 CenterZ=0 NormalX=0 NormalY=0 NormalZ=1 AngleXU=0 Radius=13 StartAngle=2.78068 EndAngle=5.92131
    g7: ArcOfCircle CenterX=21.4715 CenterY=-169.934 CenterZ=0 NormalX=0 NormalY=0 NormalZ=1 AngleXU=0 Radius=13 StartAngle=5.92268 EndAngle=9.06428
    g8: ArcOfCircle CenterX=15.1336 CenterY=-186.787 CenterZ=0 NormalX=0 NormalY=0 NormalZ=1 AngleXU=0 Radius=13 StartAngle=2.78068 EndAngle=5.92131
    g9-g12: Circle x4 (B-spline internal-alignment scaffolding for g13; pole/knot coordinates omitted)
    g13: BSplineCurve PolesCount=4 KnotsCount=2 Degree=3 IsPeriodic=0
    g14: GeomPoint X=28.8094 Y=-19.0875 Z=0
    g15: GeomPoint X=47.0443 Y=-50.4712 Z=0
    g16: Circle CenterX=53.5586 CenterY=-23.2695 CenterZ=0 NormalX=0 NormalY=0 NormalZ=1 AngleXU=0 Radius=3.24518
    g17: Circle CenterX=-195.441 CenterY=-127.082 CenterZ=0 NormalX=0 NormalY=0 NormalZ=1 AngleXU=0 Radius=1
    g18: Circle CenterX=-8.24091 CenterY=-197.481 CenterZ=0 NormalX=0 NormalY=0 NormalZ=1 AngleXU=0 Radius=1
    g19: Circle CenterX=12.8789 CenterY=-141.321 CenterZ=0 NormalX=0 NormalY=0 NormalZ=1 AngleXU=0 Radius=1
    g20: BSplineCurve PolesCount=3 KnotsCount=2 Degree=2 IsPeriodic=0
    g21: GeomPoint X=-195.441 Y=-127.082 Z=0
    g22: GeomPoint X=12.8789 Y=-141.321 Z=0
    g23: Circle CenterX=-12.8016 CenterY=-179.036 CenterZ=0 NormalX=0 NormalY=0 NormalZ=1 AngleXU=0 Radius=10.5072
    g24: Circle CenterX=0.933922 CenterY=-166.43 CenterZ=0 NormalX=0 NormalY=0 NormalZ=1 AngleXU=0 Radius=3.26661
    g25: Circle CenterX=-33.5518 CenterY=-176.44 CenterZ=0 NormalX=0 NormalY=0 NormalZ=1 AngleXU=0 Radius=5.64388
    g26: Circle CenterX=-47.2366 CenterY=-173.859 CenterZ=0 NormalX=0 NormalY=0 NormalZ=1 AngleXU=0 Radius=3.01653
    g27: Circle CenterX=-56.2595 CenterY=-171.456 CenterZ=0 NormalX=0 NormalY=0 NormalZ=1 AngleXU=0 Radius=2.12826
    g28: ArcOfCircle CenterX=51.2151 CenterY=-198.473 CenterZ=0 NormalX=0 NormalY=0 NormalZ=1 AngleXU=0 Radius=20 StartAngle=2.78189 EndAngle=4.35269
    g29: LineSegment StartX=32.4951 StartY=-191.433 StartZ=0 EndX=94.6578 EndY=-26.1352 EndZ=0
    g30: LineSegment StartX=43.1192 StartY=-220.001 StartZ=0 EndX=-196.497 EndY=-129.89 EndZ=0
    g31: LineSegment StartX=43.1192 StartY=-220.001 StartZ=0 EndX=44.1752 EndY=-217.193 EndZ=0
    g32: LineSegment StartX=117.223 StartY=-19.0875 StartZ=0 EndX=117.223 EndY=-16.0875 EndZ=0
    g33: LineSegment StartX=117.223 StartY=-16.0875 StartZ=0 EndX=17.2232 EndY=-16.0875 EndZ=0
    g34: LineSegment StartX=17.2232 StartY=-16.0875 StartZ=0 EndX=17.2232 EndY=-19.0875 EndZ=0
    g35: LineSegment StartX=28.8094 StartY=-19.0875 StartZ=0 EndX=17.2232 EndY=-19.0875 EndZ=0
    g36: LineSegment StartX=47.0443 StartY=-50.4712 StartZ=0 EndX=12.8789 EndY=-141.321 EndZ=0
    g37: LineSegment StartX=-195.441 StartY=-127.082 StartZ=0 EndX=-196.497 EndY=-129.89 EndZ=0
    g38: LineSegment StartX=85.2866 StartY=-36.8766 StartZ=0 EndX=78.9396 EndY=-53.7463 EndZ=0
    g39: LineSegment StartX=60.9579 StartY=-27.7053 StartZ=0 EndX=54.6191 EndY=-44.5532 EndZ=0
    g40: LineSegment StartX=68.0907 StartY=-82.7664 StartZ=0 EndX=61.7465 EndY=-99.6365 EndZ=0
    g41: LineSegment StartX=43.7619 StartY=-73.595 StartZ=0 EndX=37.426 EndY=-90.4435 EndZ=0
    g42: LineSegment StartX=50.885 StartY=-128.652 StartZ=0 EndX=44.5456 EndY=-145.522 EndZ=0
    g43: LineSegment StartX=26.5562 StartY=-119.481 StartZ=0 EndX=20.2251 EndY=-136.329 EndZ=0
    g44: LineSegment StartX=9.3071 StartY=-165.349 StartZ=0 EndX=2.97115 EndY=-182.197 EndZ=0
    g45: LineSegment StartX=33.6358 StartY=-174.52 StartZ=0 EndX=27.2917 EndY=-191.39 EndZ=0
  constraints (71):
    c: Block(g0)
    c: Block(g1)
    c: Block(g2)
    c: Block(g4)
    c: Block(g3)
    c: Block(g6)
    c: Block(g5)
    c: Block(g8)
    c: Block(g7)
    c: Weight(g9) = 1
    c: Equal(g9,g10)
    c: Equal(g9,g11)
    c: Equal(g9,g12)
    c: InternalAlignment(g9-g12 -> g13) x4
    c: InternalAlignment(g14,g13)
    c: InternalAlignment(g15,g13)
    c: Block(g16)
    c: Weight(g17) = 1
    c: Equal(g17,g18)
    c: Equal(g17,g19)
    c: InternalAlignment(g17,g20)
    c: InternalAlignment(g18,g20)
    c: InternalAlignment(g19,g20)
    c: InternalAlignment(g21,g20)
    c: InternalAlignment(g22,g20)
    c: Block(g20)
    c: Block(g23)
    c: Block(g24)
    c: Block(g25)
    c: Block(g26)
    c: Block(g27)
    c: Block(g28)
    c: Coincident(g29,g28)
    c: Coincident(g29,g0)
    c: Block(g13)
    c: Coincident(g31,g30)
    c: Coincident(g31,g28)
    c: Block(g31)
    c: Coincident(g32,g0)
    c: Vertical(g32)
    c: Coincident(g33,g32)
    c: Horizontal(g33)
    c: Coincident(g34,g33)
    c: Vertical(g34)
    c: Block(g33)
    c: Coincident(g35,g13)
    c: Coincident(g35,g34)
    c: Horizontal(g35)
    c: Coincident(g36,g13)
    c: Coincident(g36,g20)
    c: Coincident(g37,g20)
    c: Coincident(g37,g30)
    c: Block(g30)
    c: Coincident(g38,g1)
    c: Coincident(g38,g2)
    c: Coincident(g39,g1)
    c: Coincident(g39,g2)
    c: Coincident(g40,g3)
    c: Coincident(g40,g4)
    c: Coincident(g41,g3)
    c: Coincident(g41,g4)
    c: Coincident(g42,g5)
    c: Coincident(g42,g6)
    c: Coincident(g43,g5)
    c: Coincident(g43,g6)
    c: Coincident(g44,g7)
    c: Coincident(g44,g8)
    c: Coincident(g45,g7)
    c: Coincident(g45,g8)
    c: Distance(g30) = 256
    c: Distance(g33) = 100
FEATURE [Part::Extrusion] Extrude002
  Base = -> Sketch001
  Dir = (1,0,0)
  DirMode = 2
  FaceMakerClass = Part::FaceMakerBullseye
  LengthFwd = 8
  LengthRev = 0
  Solid = true
  Symmetric = false
FEATURE [Sketcher::SketchObject] Sketch002
  FullyConstrained = true
  sketch-geometry (20):
    g0: LineSegment StartX=-2.77179 StartY=-200.304 StartZ=0 EndX=5.22821 EndY=-200.304 EndZ=0
    g1: LineSegment StartX=5.22821 StartY=-200.304 StartZ=0 EndX=5.22821 EndY=-197.304 EndZ=0
    g2: LineSegment StartX=-2.77179 StartY=-200.304 StartZ=0 EndX=-2.77179 EndY=-197.304 EndZ=0
    g3: LineSegment StartX=5.22821 StartY=-197.304 StartZ=0 EndX=8.22821 EndY=-197.304 EndZ=0
    g4: LineSegment StartX=-2.77179 StartY=-197.304 StartZ=0 EndX=-5.77179 EndY=-197.304 EndZ=0
    g5: LineSegment StartX=19.2282 StartY=-203.304 StartZ=0 EndX=19.2282 EndY=-206.304 EndZ=0
    g6: LineSegment StartX=-16.7718 StartY=-203.304 StartZ=0 EndX=-16.7718 EndY=-206.304 EndZ=0
    g7: LineSegment StartX=-16.7718 StartY=-206.304 StartZ=0 EndX=19.2282 EndY=-206.304 EndZ=0
    g8: Circle CenterX=-16.7718 CenterY=-203.304 CenterZ=0 NormalX=0 NormalY=0 NormalZ=1 AngleXU=0 Radius=1
    g9: Circle CenterX=-5.77179 CenterY=-203.304 CenterZ=0 NormalX=0 NormalY=0 NormalZ=1 AngleXU=0 Radius=1
    g10: Circle CenterX=-5.77179 CenterY=-197.304 CenterZ=0 NormalX=0 NormalY=0 NormalZ=1 AngleXU=0 Radius=1
    g11: BSplineCurve PolesCount=3 KnotsCount=2 Degree=2 IsPeriodic=0
    g12: GeomPoint X=-16.7718 Y=-203.304 Z=0
    g13: GeomPoint X=-5.77179 Y=-197.304 Z=0
    g14: Circle CenterX=19.2282 CenterY=-203.304 CenterZ=0 NormalX=0 NormalY=0 NormalZ=1 AngleXU=0 Radius=1
    g15: Circle CenterX=8.22821 CenterY=-203.304 CenterZ=0 NormalX=0 NormalY=0 NormalZ=1 AngleXU=0 Radius=1
    g16: Circle CenterX=8.22821 CenterY=-197.304 CenterZ=0 NormalX=0 NormalY=0 NormalZ=1 AngleXU=0 Radius=1
    g17: BSplineCurve PolesCount=3 KnotsCount=2 Degree=2 IsPeriodic=0
    g18: GeomPoint X=19.2282 Y=-203.304 Z=0
    g19: GeomPoint X=8.22821 Y=-197.304 Z=0
  constraints (41):
    c: Horizontal(g0)
    c: Distance(g0) = 8
    c: Coincident(g1,g0)
    c: Vertical(g1)
    c: Distance(g1) = 3
    c: Coincident(g2,g0)
    c: Vertical(g2)
    c: Distance(g2) = 3
    c: Coincident(g3,g1)
    c: Horizontal(g3)
    c: Distance(g3) = 3
    c: Coincident(g4,g2)
    c: Horizontal(g4)
    c: Distance(g4) = 3
    c: Vertical(g5)
    c: Vertical(g6)
    c: Coincident(g7,g6)
    c: Coincident(g7,g5)
    c: Weight(g8) = 1
    c: Equal(g8,g9)
    c: Equal(g8,g10)
    c: Coincident(g11,g4)
    c: InternalAlignment(g8,g11)
    c: InternalAlignment(g9,g11)
    c: InternalAlignment(g10,g11)
    c: InternalAlignment(g12,g11)
    c: InternalAlignment(g13,g11)
    c: Coincident(g17,g5)
    c: Weight(g14) = 1
    c: Equal(g14,g15)
    c: Equal(g14,g16)
    c: Coincident(g17,g3)
    c: InternalAlignment(g14,g17)
    c: InternalAlignment(g15,g17)
    c: InternalAlignment(g16,g17)
    c: InternalAlignment(g18,g17)
    c: InternalAlignment(g19,g17)
    c: Block(g7)
    c: Block(g17)
    c: Block(g11)
    c: Block(g6)
FEATURE [Part::Extrusion] Extrude003
  Base = -> Sketch002
  Dir = (0,0,1)
  DirMode = 2
  FaceMakerClass = Part::FaceMakerBullseye
  LengthFwd = 260
  LengthRev = 0
  Solid = true
  Symmetric = false
FEATURE [Part::Extrusion] Extrude
  Base = -> Sketch
  Dir = (0,0,1)
  DirMode = 2
  FaceMakerClass = Part::FaceMakerBullseye
  LengthFwd = 14
  LengthRev = 0
  Solid = true
  Symmetric = false
